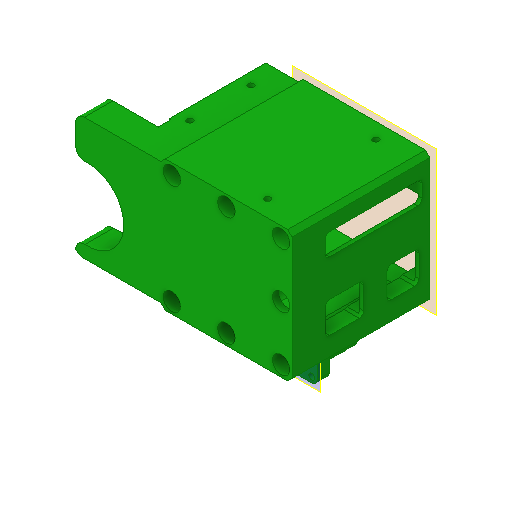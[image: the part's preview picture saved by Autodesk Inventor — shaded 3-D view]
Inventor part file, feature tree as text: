
AUTODESK INVENTOR PART (.ipt)
format: ipt  version: 2022 (Build 260153000, 153)  size: 549,376 bytes
history: native  units: mm
features: reference x22, sketch x14, other x13, extrude x10, plane x5, projected_geometry x5, hole x4, fillet x3
ambient origin geometry x8: Origin, YZ Plane, XZ Plane, XY Plane, X Axis, Y Axis, Z Axis, Center Point
bodies: Solid1 (feature_tree)
feature tree (76):
  plane  "Work Plane1"
  plane  "Arbeitsebene4"
  extrude  "Extrusion1"  Depth=10.0mm TaperAngle=0.0deg
  extrude  "Extrusion3"  Depth=5.0mm TaperAngle=0.0deg
  extrude  "Extrusion4"  Depth=10.0mm TaperAngle=0.0deg
  extrude  "Extrusion6"  Depth=4.0mm
  hole  "Hole1"  [1 undecoded]
  plane  "Arbeitsebene3"
  extrude  "Extrusion7"  Depth=3.0mm
  sketch  "Skizze12"  dims[d58=10.0mm d59=0.0mm d60=2.0mm]
  plane  "Arbeitsebene5"
  extrude  "Extrusion10"  Depth=2.0mm
  fillet  "Rundung1"  Radius=2.0mm
  hole  "Bohrung3"  [1 undecoded]
  extrude  "Extrusion12"  Depth=10.0mm TaperAngle=0.0deg
  fillet  "Rundung2"  Radius=60.0mm
  hole  "Bohrung4"  [1 undecoded]
  sketch  "Skizze17"  dims[d81=10.0mm]
  plane  "Arbeitsebene6"
  extrude  "Extrusion13"  Depth=24.0mm
  extrude  "Extrusion14"  TaperAngle=0.0deg  [1 undecoded]
  hole  "Bohrung5"  [1 undecoded]
  fillet  "Rundung3"  [1 undecoded]
  extrude  "Extrusion15"  [1 undecoded]
  sketch  "Sketch1"  dims[d0=5.0mm d1=0.0mm d7=10.0mm d8=0.0mm]
  reference  "Reference1"
  reference  "Reference2"
  reference  "Reference3"
  sketch  "Sketch3"  dims[d10=40.0mm d11=0.0mm d14=5.0mm d15=0.0mm]
  projected_geometry  "Projected Loop2"
  sketch  "Sketch4"  dims[d16=2.9mm d17=6.0mm d18=19.05mm d19=4.775mm d20=14.3117mm d21=20.0mm d22=20.594885mm d26=10.0mm d27=0.0mm]
  sketch  "Sketch6"  dims[d41=10.0mm d42=0.0mm d43=4.0mm]
  projected_geometry  "Projected Loop4"
  sketch  "Sketch7"  dims[d48=4.5mm d49=6.0mm d50=8.0mm d51=55.0mm d52=90.0deg d53=60.0mm d54=20.594885mm d55=6.0mm]
  reference  "Reference5"
  reference  "Reference6"
  reference  "Reference8"
  reference  "Reference9"
  reference  "Reference10"
  sketch  "Skizze8"  dims[d56=6.0mm d57=3.0mm]
  reference  "Referenz11"
  reference  "Referenz12"
  reference  "Referenz13"
  reference  "Referenz14"
  reference  "Referenz15"
  reference  "Referenz16"
  projected_geometry  "Projizierte Kontur9"
  reference  "Referenz18"
  sketch  "Skizze14"  dims[d61=2.8mm d62=6.0mm d63=8.0mm d64=55.0mm d65=90.0deg d66=60.0mm d67=0.0mm d68=2.0mm]
  projected_geometry  "Projizierte Kontur11"
  projected_geometry  "Projizierte Kontur12"
  sketch  "Skizze15"  dims[d69=2.0mm d70=2.0mm]
  sketch  "Skizze16"  dims[d71=2.0mm d72=10.0mm d73=0.0mm d76=60.0mm d77=0.0mm]
  reference  "Referenz20"
  reference  "Referenz21"
  reference  "Referenz22"
  reference  "Referenz23"
  sketch  "Skizze18"  dims[d82=2.8mm d83=6.0mm d84=5.0mm d85=13.0mm d86=90.0deg d87=8.0mm d88=20.594885mm d89=5.0mm]
  reference  "Referenz24"
  sketch  "Skizze19"  dims[d90=33.0mm d91=24.0mm]
  sketch  "Skizze20"  dims[d92=0.0mm d93=0.0mm d94=0.0mm]
  reference  "Referenz26"
  reference  "Referenz27"
  other  "<userpath>\Documents\GitHub\cellstorm\INVENTOR\cellSTORM_v6.iam"
  other  "cellSTORM_v6.iam"
  other  "00_XY_stage-CHUO_SEIKI_LD-647-R1:2"
  other  "00_XY_stage-CHUO_SEIKI_LD-647-R1-Bottom:1"
  other  "cellSTORM_v5_microsocpe:1"
  other  "00_NEMA11:1"
  other  "cellSTORM_v5_cellphone_craddle:1"
  other  "00_Arduino_CNC_Assembly:1"
  other  "Arduino_Uno_1"
  other  "Arduino UNO Rev.3 (CH340)-CAWEB.ORG.stp_3"
  other  "PCB.stp_4"
  other  "cellSTORM_v5_opticalstage:1"
  other  "<userpath>\Dropbox\cellSTORM\cellSTORM_v6.iam"
note: 7 required parameter values undecoded (feature->parameter linkage not recoverable at this tier; creation-order binding heuristic only, values carry confidence <= 0.55)
